FCSTD DOCUMENT  (FreeCAD 0.16R6223 (Git))
Label: velokey
License: All rights reserved
LicenseURL: http://en.wikipedia.org/wiki/All_rights_reserved
objects: Sketcher::SketchObject×1
note: 1 computed .brp shape members not serialized (recipe doc carries the construction recipe); baked Part::Feature solids carry a one-line shape summary decoded from their .brp

FEATURE [Sketcher::SketchObject] Sketch
  sketch-geometry (6):
    g0: ArcOfCircle CenterX=-49.6 CenterY=0 CenterZ=0 NormalX=0 NormalY=0 NormalZ=1 Radius=17.5 StartAngle=1.5708 EndAngle=4.10612
    g1: ArcOfCircle CenterX=49.6 CenterY=0 CenterZ=0 NormalX=0 NormalY=0 NormalZ=1 Radius=17.5 StartAngle=5.31866 EndAngle=7.85398
    g2: ArcOfCircle CenterX=0 CenterY=-35 CenterZ=0 NormalX=0 NormalY=0 NormalZ=1 Radius=17 StartAngle=4.10612 EndAngle=5.31866
    g3: LineSegment StartX=-49.6 StartY=17.5 StartZ=0 EndX=49.6 EndY=17.5 EndZ=0
    g4: LineSegment StartX=-59.5716 StartY=-14.3812 StartZ=0 EndX=-9.68668 EndY=-48.9703 EndZ=0
    g5: LineSegment StartX=59.5716 StartY=-14.3812 StartZ=0 EndX=9.68668 EndY=-48.9703 EndZ=0
  constraints (19):
    c: PointOnObject(g0,g-1)
    c: PointOnObject(g1,g-1)
    c: Radius(g1) = 17.5
    c: DistanceX(g-1,g0) = -49.6
    c: DistanceX(g-1,g1) = 49.6
    c: DistanceY(g-1,g2) = -35
    c: Radius(g2) = 17
    c: DistanceX(g-1,g2) = 0
    c: Horizontal(g3)
    c: Symmetric(g3,g3,g-2)
    c: Coincident(g0,g3)
    c: Coincident(g1,g3)
    c: Coincident(g4,g0)
    c: Coincident(g5,g1)
    c: DistanceX(g0,g0) = 9.97158
    c: DistanceX(g1,g1) = 9.97158
    c: Coincident(g5,g2)
    c: Coincident(g4,g2)
    c: Coincident(g-1,g-1)
